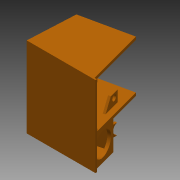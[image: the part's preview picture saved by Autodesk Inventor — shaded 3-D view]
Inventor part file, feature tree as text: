
AUTODESK INVENTOR PART (.ipt)
format: ipt  version: 2015 SP2 (Build 190223200, 223)  size: 511,488 bytes
history: native  units: mm
features: sketch x29, extrude x23, projected_geometry x18, plane x16, hole x6, fillet x1
ambient origin geometry x8: Origin, YZ Plane, XZ Plane, XY Plane, X Axis, Y Axis, Z Axis, Center Point
bodies: Volumenkörper1 (feature_tree)
feature tree (93):
  sketch  "Skizze1"  dims[d2=6.0mm d3=6.0mm]
  extrude  "Extrusion1"  Depth=6.0mm
  extrude  "Extrusion2"  Depth=35.0mm
  extrude  "Extrusion3"  Depth=15.5mm
  sketch  "Skizze2"  dims[d4=6.0mm d5=35.0mm]
  plane  "Arbeitsebene2"
  extrude  "Extrusion5"  Depth=2.0mm TaperAngle=0.0deg
  plane  "Arbeitsebene3"
  sketch  "Skizze9"  dims[d9=29.0mm d10=2.0mm d11=0.0mm]
  extrude  "Extrusion9"  Depth=4.0mm
  plane  "Arbeitsebene4"
  extrude  "Extrusion10"  Depth=4.0mm
  plane  "Arbeitsebene6"
  plane  "Arbeitsebene7"
  extrude  "Extrusion11"  Depth=4.0mm
  plane  "Arbeitsebene8"
  extrude  "Extrusion12"  TaperAngle=0.0deg  [1 undecoded]
  extrude  "Extrusion13"  Depth=23.0mm
  extrude  "Extrusion14"  Depth=3.0mm
  extrude  "Extrusion15"  Depth=4.0mm
  extrude  "Extrusion17"  TaperAngle=75.0deg  [1 undecoded]
  extrude  "Extrusion18"  Depth=25.0mm
  extrude  "Extrusion19"  Depth=18.0mm
  extrude  "Extrusion20"  TaperAngle=15.0deg  [1 undecoded]
  extrude  "Extrusion21"  [1 undecoded]
  extrude  "Extrusion22"  Depth=20.0mm
  plane  "Arbeitsebene10"
  hole  "Bohrung1"  [1 undecoded]
  plane  "Arbeitsebene11"
  sketch  "Skizze31"  dims[d61=4.0mm d62=0.0mm d63=4.0mm d64=0.0mm]
  extrude  "Extrusion23"  Depth=4.0mm
  extrude  "Extrusion24"  Depth=4.0mm TaperAngle=0.0deg
  hole  "Bohrung2"  [1 undecoded]
  hole  "Bohrung3"  [1 undecoded]
  extrude  "Extrusion25"  Depth=3.0mm
  plane  "Arbeitsebene14"
  sketch  "Skizze37"  dims[d78=18.0mm d79=4.0mm]
  sketch  "Skizze38"  dims[d82=7.0mm d83=3.0mm]
  plane  "Arbeitsebene15"
  sketch  "Skizze39"  dims[d84=23.0mm d86=15.0mm d87=0.0mm]
  plane  "Arbeitsebene16"
  sketch  "Skizze40"  dims[d88=10.0mm d89=15.0mm d90=0.0mm]
  plane  "Arbeitsebene17"
  hole  "Bohrung5"  [1 undecoded]
  extrude  "Extrusion26"  Depth=15.0mm TaperAngle=0.0deg
  hole  "Bohrung6"  [1 undecoded]
  hole  "Bohrung7"  [1 undecoded]
  extrude  "Extrusion27"  Depth=3.0mm
  fillet  "Rundung1"  Radius=15.0mm
  plane  "Arbeitsebene18"
  extrude  "Extrusion28"  Depth=3.0mm TaperAngle=0.0deg
  sketch  "Skizze5"  dims[d6=100.0mm d7=15.5mm]
  sketch  "Skizze10"  dims[d12=5.0mm d13=0.0mm d14=4.0mm]
  sketch  "Skizze13"  dims[d15=4.0mm d16=9.0mm]
  sketch  "Skizze14"  dims[d17=4.0mm d23=85.0mm]
  sketch  "Skizze15"  dims[d25=9.0mm d26=0.0mm]
  sketch  "Skizze16"  dims[d27=3.0mm d28=23.0mm]
  sketch  "Skizze17"  dims[d29=3.0mm d30=57.0mm]
  projected_geometry  "Projizierte Kontur6"
  sketch  "Skizze20"  dims[d31=80.0mm d32=0.0mm d35=4.0mm]
  projected_geometry  "Projizierte Kontur8"
  sketch  "Skizze24"  dims[d37=4.0mm d38=0.0mm d39=75.0deg]
  projected_geometry  "Projizierte Kontur11"
  sketch  "Skizze25"  dims[d46=20.0mm d47=0.0mm d48=25.0mm]
  sketch  "Skizze26"  dims[d49=30.0mm d50=0.0mm d51=18.0mm]
  sketch  "Skizze27"  dims[d52=20.0mm d53=15.0deg]
  projected_geometry  "Projizierte Kontur12"
  sketch  "Skizze28"  dims[d54=30.0mm d55=0.0mm d56=-25.0mm]
  projected_geometry  "Projizierte Kontur13"
  plane  "Arbeitsebene9"
  sketch  "Skizze30"  dims[d58=30.0mm d59=0.0mm d60=20.0mm]
  projected_geometry  "Projizierte Kontur15"
  projected_geometry  "Projizierte Kontur16"
  sketch  "Skizze32"  dims[d65=4.0mm d66=0.0mm d69=4.0mm]
  projected_geometry  "Projizierte Kontur17"
  sketch  "Skizze33"  dims[d70=4.0mm d71=0.0mm d72=100.0mm d73=0.0mm]
  projected_geometry  "Projizierte Kontur18"
  sketch  "Skizze34"  dims[d74=100.0mm d75=0.0mm d76=100.0mm d77=0.0mm]
  projected_geometry  "Projizierte Kontur19"
  projected_geometry  "Projizierte Kontur20"
  projected_geometry  "Projizierte Kontur21"
  plane  "Arbeitsebene12"
  plane  "Arbeitsebene13"
  projected_geometry  "Projizierte Kontur22"
  sketch  "Skizze41"  dims[d91=-10.471976mm d92=0.0mm]
  sketch  "Skizze42"  dims[d93=12.7mm d94=6.0mm d95=4.0mm d96=2.0mm d97=90.0deg d98=8.0mm d99=20.594885mm d100=180.0deg]
  projected_geometry  "Projizierte Kontur23"
  projected_geometry  "Projizierte Kontur24"
  sketch  "Skizze44"  dims[d101=5.0mm d102=3.0mm d103=15.0mm]
  projected_geometry  "Projizierte Kontur25"
  projected_geometry  "Projizierte Kontur26"
  sketch  "Skizze48"  dims[d104=12.0mm d105=3.0mm d106=10.0mm d107=0.0mm d108=0.0mm d112=3.0mm d113=0.0mm d115=8.0mm d116=7.2mm d117=6.0mm d118=4.0mm d119=2.0mm d120=90.0deg d121=8.0mm d122=20.594885mm d123=6.0mm d124=6.0mm d125=2.459mm d126=6.0mm d127=4.0mm d128=2.0mm d129=90.0deg d130=7.0mm d131=20.594885mm d132=9.3mm d133=11.3mm d134=5.0mm d135=6.6mm d136=20.0mm d138=15.0mm d139=5.0mm d140=0.0mm d141=60.0deg d142=14.0mm d143=90.0deg d151=60.0deg d152=6.108652mm d153=3.0mm d154=6.0mm d155=4.0mm d156=2.0mm d157=90.0deg d158=36.0mm d159=20.594885mm d164=11.0mm d165=11.0mm d166=11.0mm d167=5.0mm d168=0.0mm d169=2.013mm d170=3.0mm d171=4.0mm d172=2.0mm d173=90.0deg d174=4.0mm d175=20.594885mm d176=2.459mm d177=3.0mm d178=4.0mm d179=2.0mm d180=90.0deg d181=4.0mm d182=20.594885mm d183=3.0mm d184=2.0mm d185=0.0mm d186=100.0mm d187=6.5mm d188=9.0mm d189=2.0mm d190=0.0mm d191=11.0mm d192=90.0deg d193=20.0mm d194=0.0mm d160=1.0mm d161=1.0mm]
  projected_geometry  "Projizierte Kontur30"
note: 10 required parameter values undecoded (feature->parameter linkage not recoverable at this tier; creation-order binding heuristic only, values carry confidence <= 0.55)
